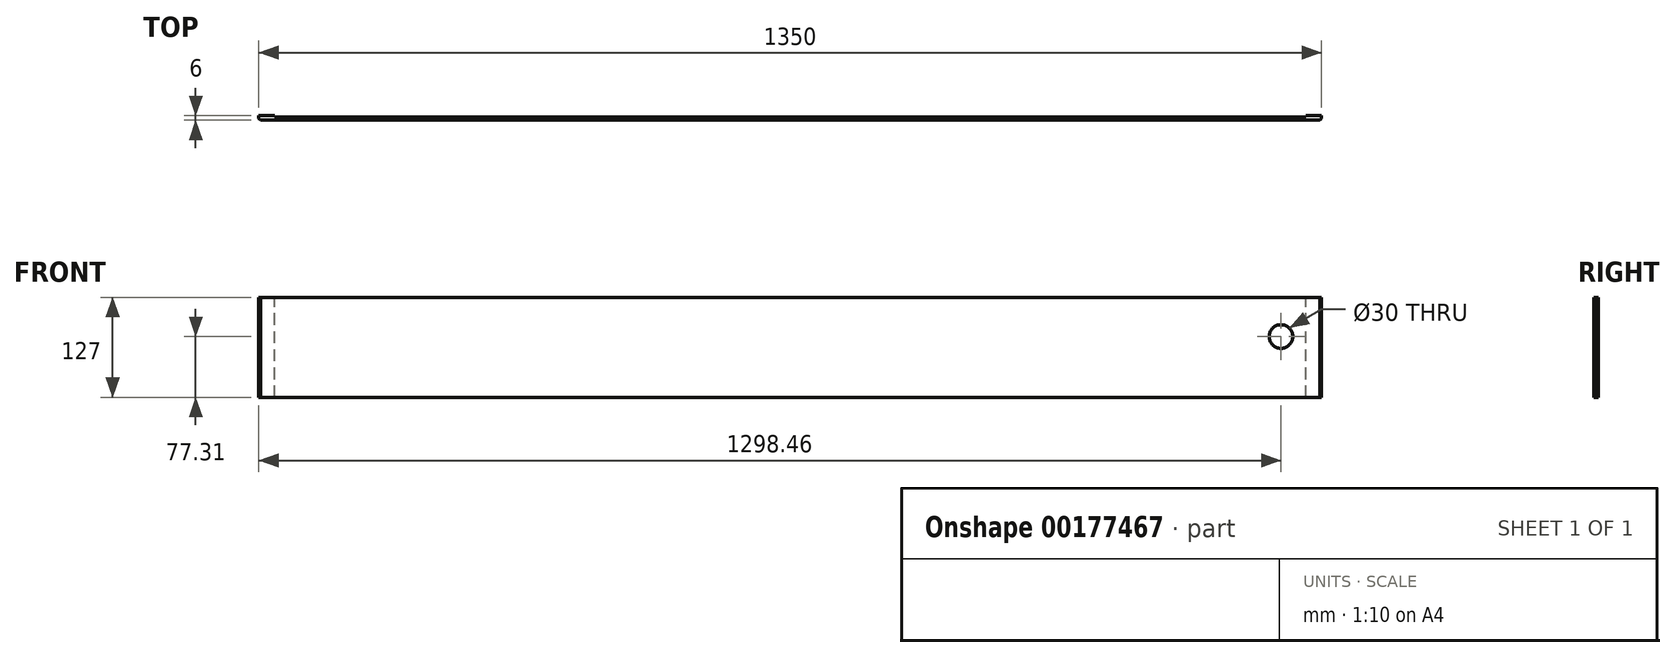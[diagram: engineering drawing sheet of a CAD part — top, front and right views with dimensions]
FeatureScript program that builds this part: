
annotation { "Feature Type Name" : "Feature", "Feature Type Description" : "" }
export const myFeature = defineFeature(function(context is Context, id is Id, definition is map)
    precondition{}
    {
        {
            var Q0;
            Q0=qCreatedBy(makeId("Front.planeOp"),FACE);
            var sketch = newSketch(context, id + "F0", { "sketchPlane" : qUnion([Q0])});
            skLineSegment(sketch, "E0.bottom", {"start": v(675, -63.5) * mm, "end": v(-675, -63.5) * mm});
            skLineSegment(sketch, "E0.top", {"start": v(675, 63.5) * mm, "end": v(-675, 63.5) * mm});
            skLineSegment(sketch, "E0.left", {"start": v(675, -63.5) * mm, "end": v(675, 63.5) * mm});
            skLineSegment(sketch, "E0.right", {"start": v(-675, -63.5) * mm, "end": v(-675, 63.5) * mm});
            skPoint(sketch, "E0.middle", {"position": v(0, 0) * mm});
            skPoint(sketch, "E1", {"position": v(623.46, 13.81) * mm});
            skLineSegment(sketch, "E2.0", {"start": v(-655, -63.5) * mm, "end": v(-655, 63.5) * mm});
            skLineSegment(sketch, "E3.0", {"start": v(655, -63.5) * mm, "end": v(655, 63.5) * mm});
            skSolve(sketch);
        }
        {
            var Q0;
            {var subQ0=sQuery(id+"F0.wireOp",EDGE,"E0.right");Q0=makeQuery(id+"F0.imprint","IMPRINT",FACE,{"disambiguationData":[TD([[makeQuery(id+"F0.imprint","IMPRINT",EDGE,{"derivedFrom":subQ0}),-1.0]])]});}
            var Q1;
            {var subQ0=sQuery(id+"F0.wireOp",EDGE,"E2.0");Q1=makeQuery(id+"F0.imprint","IMPRINT",FACE,{"disambiguationData":[TD([[makeQuery(id+"F0.imprint","IMPRINT",EDGE,{"derivedFrom":subQ0}),-1.0]])]});}
            var Q2;
            {var subQ0=sQuery(id+"F0.wireOp",EDGE,"E0.left");Q2=makeQuery(id+"F0.imprint","IMPRINT",FACE,{"disambiguationData":[TD([[makeQuery(id+"F0.imprint","IMPRINT",EDGE,{"derivedFrom":subQ0}),1.0]])]});}
            extrude(context, id + "F1", {"entities" : qUnion([Q0, Q1, Q2]), "depth" : 4 * mm});
        }
        {
            var Q0;
            {var subQ0=sQuery(id+"F0.wireOp",EDGE,"E0.right");Q0=makeQuery(id+"F0.imprint","IMPRINT",FACE,{"disambiguationData":[TD([[makeQuery(id+"F0.imprint","IMPRINT",EDGE,{"derivedFrom":subQ0}),-1.0]])]});}
            var Q1;
            {var subQ0=sQuery(id+"F0.wireOp",EDGE,"E0.left");Q1=makeQuery(id+"F0.imprint","IMPRINT",FACE,{"disambiguationData":[TD([[makeQuery(id+"F0.imprint","IMPRINT",EDGE,{"derivedFrom":subQ0}),1.0]])]});}
            extrude(context, id + "F2", {"entities" : qUnion([Q0, Q1]), "operationType" : NewBodyOperationType.ADD, "oppositeDirection" : true, "depth" : 2 * mm});
        }
        {
            var Q0;
            Q0=sQuery(id+"F0.wireOp",VERTEX,"E1");
            var Q1;
            Q1=makeQuery(id+"F1.opExtrude","SWEPT_BODY",BODY,{"disambiguationData":[OSD([sQuery(id+"F0.wireOp",EDGE,"E0.bottom"),sQuery(id+"F0.wireOp",EDGE,"E0.top"),sQuery(id+"F0.wireOp",EDGE,"E0.right"),sQuery(id+"F0.wireOp",EDGE,"E3.0")])]});
            hole(context, id + "F3", {"style" : HoleStyle.SIMPLE, "endStyle" : HoleEndStyle.THROUGH, "oppositeDirection" : true, "holeDiameter" : 30 * mm, "locations" : qUnion([Q0]), "scope" : qUnion([Q1]), "isTappedThrough" : true});
        }
        {
            var Q0;
            Q0=makeQuery(id+"F1.opExtrude","CAP_EDGE",EDGE,{"disambiguationData":[OSD([sQuery(id+"F0.wireOp",EDGE,"E0.left")])],"isStart":false});
            var Q1;
            Q1=makeQuery(id+"F1.opExtrude","CAP_EDGE",EDGE,{"disambiguationData":[OSD([sQuery(id+"F0.wireOp",EDGE,"E0.right")])],"isStart":false});
            chamfer(context, id + "F4", {"entities" : qUnion([Q0, Q1]), "width" : 2 * mm, "tangentPropagation" : true});
        }
    });
